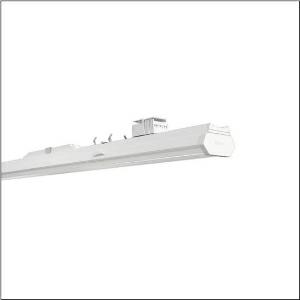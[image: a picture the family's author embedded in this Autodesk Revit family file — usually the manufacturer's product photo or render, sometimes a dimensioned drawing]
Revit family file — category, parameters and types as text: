
# Revit family: licross_r__11_protected_mo_51tp11mn495g_eae0
name_source: partatom
category: Lighting Fixtures
units: mm (PartAtom-declared; Revit-internal decimal feet)

## family parameters
Cut with Voids When Loaded = No
Host = Face
Light Source = No
Part Type = Normal
Room Calculation Point = No
Round Connector Dimension = Use Diameter
Shared = No

## types (1)
- --- (1 x LED, 9980 lm, 55.3 W, 4000K)
    Apparent Load = 55 VA
    CIE Flux Codes = 83 94 98 100 100
    Color Rendering = 80
    Color Temperature = 4000K
    Default Elevation = 1800 mm
    Description = Licross® 11 Protected MO, luminaire insert, of sheet steel, galvanised, coil coated, white, length: 1.500mm, width: 90mm, height: 101mm, LED rated luminous flux: 9.980lm, light colour: 840, control gear: ON/OFF Multilumen, with plug, 3-pole, with phase selection, mains connection: 220..240V, AC, 50/60Hz, rated input power: 55W, internal wiring halogen-free, primary light control with lens, of plastic, primary optical cover: cover, of PMMA, light emission: direct distribution, primary light characteristic: symmetric, protection rating (complete): IP64, insulation class (complete): insulation class I (protective earthing), certification: CE, ENEC, VDE, UKCA, protection symbol: D if used in an environment with conductive dust loads with corresponding accessories, impact resistance: IK06, permissible ambient temperature for indoor applications: -35..+40°C, corresponds to IFS (International Featured Standards) requirements for safety and quality in the food industry, reducing of maximum allowable ambient temperature of 5°C with ceiling mounting, LABS conformity tested according to VDMA 24364:2018-05, packaging unit: 1 piece
    Height = 92 mm
    Lamp = 1 x LED
    Lamp Light Flux = 9980 lm
    Lamp Power = 55.3 W
    Lamp count = 1
    Length = 1500 mm
    Luminous efficacy = 180 lm/W
    Manufacturer = Siteco
    ModVariant = No
    Model = 51TP11MN495G
    Mounting Place = Ceiling
    Mounting Type = Pendant
    Number of Poles = 1
    OnlyDefault = Yes
    Power Factor = 1
    Product Name = Licross® 11 Protected MO
    Product group = luminaire insert | ceiling pendant
    ProductGroupID = 902
    Protection Class = Protection class I
    Protection Degree = IP 64
    RLX_Detail_Level = 1
    RLX_Emergency_Light_Flux = 0 lm
    RLX_Emergency_Type = 0
    RLX_Emergency_Type_DB = No
    RlxData = <blob elided: 21905 chars, md5=1f1e4974>
    Socket = socket
    Standby Power = 0 W
    System Light Flux = 9980 lm
    System Power = 55 W
    Type Comments = factory setting: luminous flux: 100 % | (A | C | E) | 126 mA
    Type Image = l_1256148.jpg
    URL = http://relux.com
    VarID = @adj_107291
    Voltage = 0 V
    Weight = 0.00 kg
    Width = 88 mm

## geometry (parser evidence)
native form markers: Blend x4, Sweep x12
no freeform markers — native parametric forms only
